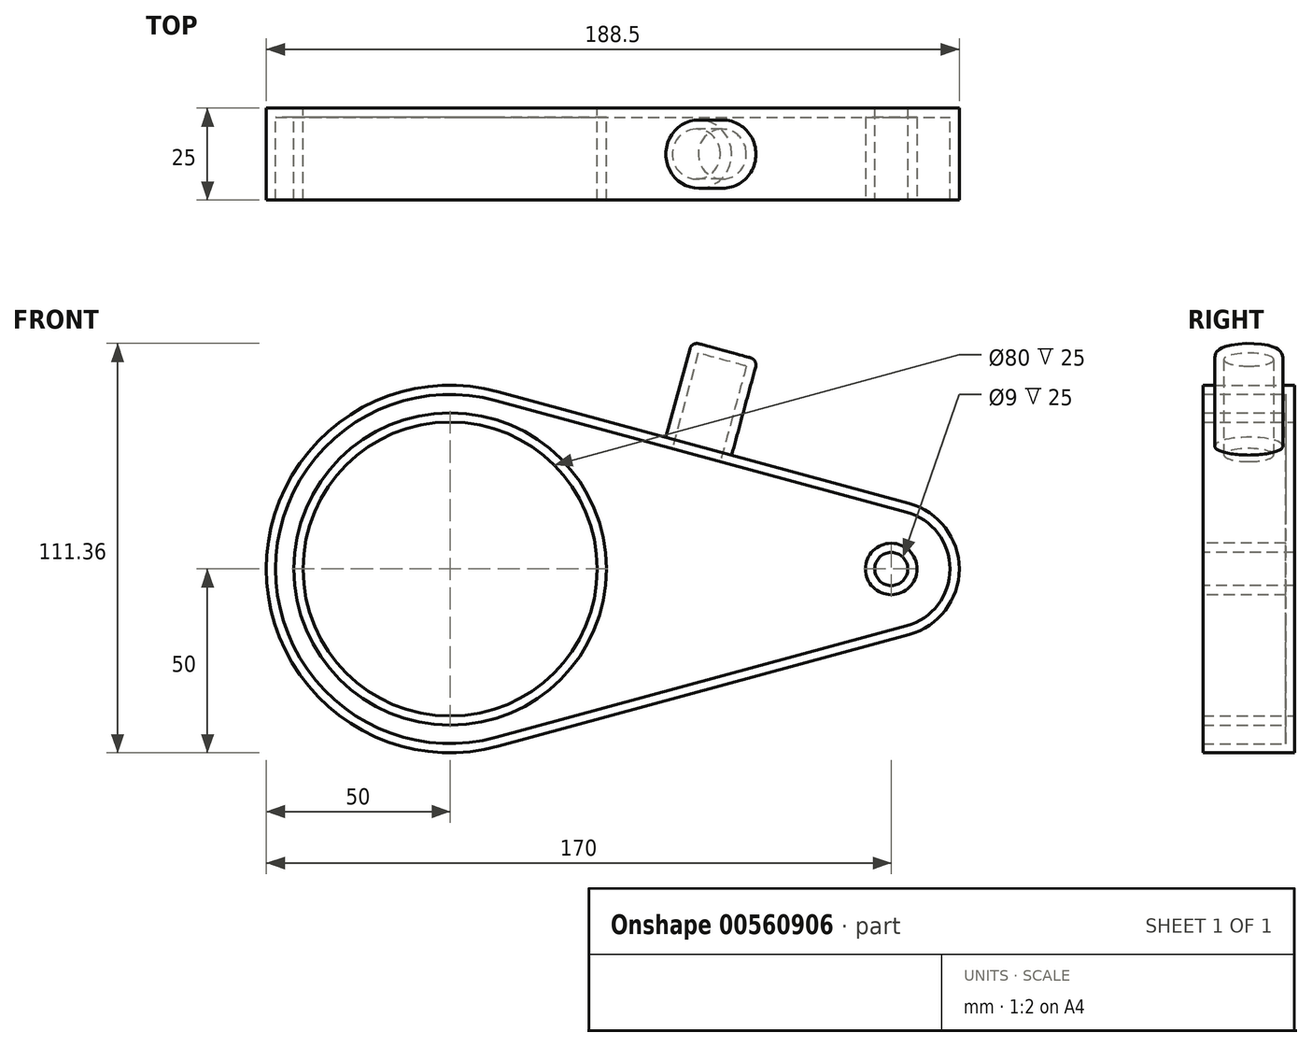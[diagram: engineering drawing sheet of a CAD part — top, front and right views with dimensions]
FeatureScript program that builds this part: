
annotation { "Feature Type Name" : "Feature", "Feature Type Description" : "" }
export const myFeature = defineFeature(function(context is Context, id is Id, definition is map)
    precondition{}
    {
        {
            var Q0;
            Q0=qCreatedBy(makeId("Front.planeOp"),FACE);
            var sketch = newSketch(context, id + "F0", { "sketchPlane" : qUnion([Q0])});
            skCircle(sketch, "E0", {"center": v(0, 0) * mm, "radius": 50 * mm});
            skCircle(sketch, "E1", {"center": v(120, 0) * mm, "radius": 18.5 * mm});
            skLineSegment(sketch, "E2", {"start": v(13.13, 48.25) * mm, "end": v(124.86, 17.85) * mm});
            skLineSegment(sketch, "E3", {"start": v(13.13, -48.25) * mm, "end": v(124.86, -17.85) * mm});
            skCircle(sketch, "E4", {"center": v(0, 0) * mm, "radius": 40 * mm});
            skSolve(sketch);
        }
        {
            var Q0;
            Q0 = qSketchRegion(id + "F0", true);
            extrude(context, id + "F1", {"entities" : qUnion([Q0]), "depth" : 25 * mm, "offsetDistance" : 25 * mm});
        }
        {
            var Q0;
            Q0=makeQuery(id+"F1.opExtrude","SWEPT_FACE",FACE,{"disambiguationData":[OSD([sQuery(id+"F0.wireOp",EDGE,"E2")])]});
            var sketch = newSketch(context, id + "F2", { "sketchPlane" : qUnion([Q0])});
            skCircle(sketch, "E5", {"center": v(56.48, -12.5) * mm, "radius": 9.28 * mm});
            skPoint(sketch, "E5.centerSnap0", {"position": v(0, -12.5) * mm});
            skSolve(sketch);
        }
        {
            var Q0;
            Q0 = qSketchRegion(id + "F2", true);
            extrude(context, id + "F3", {"entities" : qUnion([Q0]), "operationType" : NewBodyOperationType.ADD, "depth" : 26.9 * mm, "offsetDistance" : 25 * mm});
        }
        {
            var Q0;
            Q0=makeQuery(id+"F3.opExtrude","CAP_FACE",FACE,{"disambiguationData":[OSD([sQuery(id+"F2.wireOp",EDGE,"E5")])],"isStart":false});
            var Q1;
            Q1=makeQuery(id+"F3.opExtrude","CAP_EDGE",EDGE,{"disambiguationData":[OSD([sQuery(id+"F2.wireOp",EDGE,"E5")])],"isStart":true});
            fillet(context, id + "F4", {"entities" : qUnion([Q0, Q1]), "radius" : 2 * mm, "tangentPropagation" : true, "allowEdgeOverflow" : false});
        }
        {
            var Q0;
            Q0=makeQuery(id+"F1.opExtrude","CAP_FACE",FACE,{"disambiguationData":[OSD([sQuery(id+"F0.wireOp",EDGE,"E0"),sQuery(id+"F0.wireOp",EDGE,"E1"),sQuery(id+"F0.wireOp",EDGE,"E2"),sQuery(id+"F0.wireOp",EDGE,"E3"),sQuery(id+"F0.wireOp",EDGE,"E4")])],"isStart":false});
            var sketch = newSketch(context, id + "F5", { "sketchPlane" : qUnion([Q0])});
            skCircle(sketch, "E6", {"center": v(120, 0) * mm, "radius": 4.5 * mm});
            skSolve(sketch);
        }
        {
            var Q0;
            Q0=makeQuery(id+"F5.imprint","IMPRINT",FACE,{"disambiguationData":[TD([[makeQuery(id+"F5.imprint","IMPRINT",EDGE,{"derivedFrom":sQuery(id+"F5.wireOp",EDGE,"E6")}),1.0]])]});
            extrude(context, id + "F6", {"entities" : qUnion([Q0]), "operationType" : NewBodyOperationType.REMOVE, "endBound" : BoundingType.THROUGH_ALL, "oppositeDirection" : true, "depth" : 25 * mm, "offsetDistance" : 25 * mm});
        }
        {
            var Q0;
            Q0=makeQuery(id+"F1.opExtrude","CAP_FACE",FACE,{"disambiguationData":[OSD([sQuery(id+"F0.wireOp",EDGE,"E0"),sQuery(id+"F0.wireOp",EDGE,"E1"),sQuery(id+"F0.wireOp",EDGE,"E2"),sQuery(id+"F0.wireOp",EDGE,"E3"),sQuery(id+"F0.wireOp",EDGE,"E4")])],"isStart":false});
            shell(context, id + "F7", {"entities" : qUnion([Q0]), "thickness" : 2.5 * mm});
        }
    });
